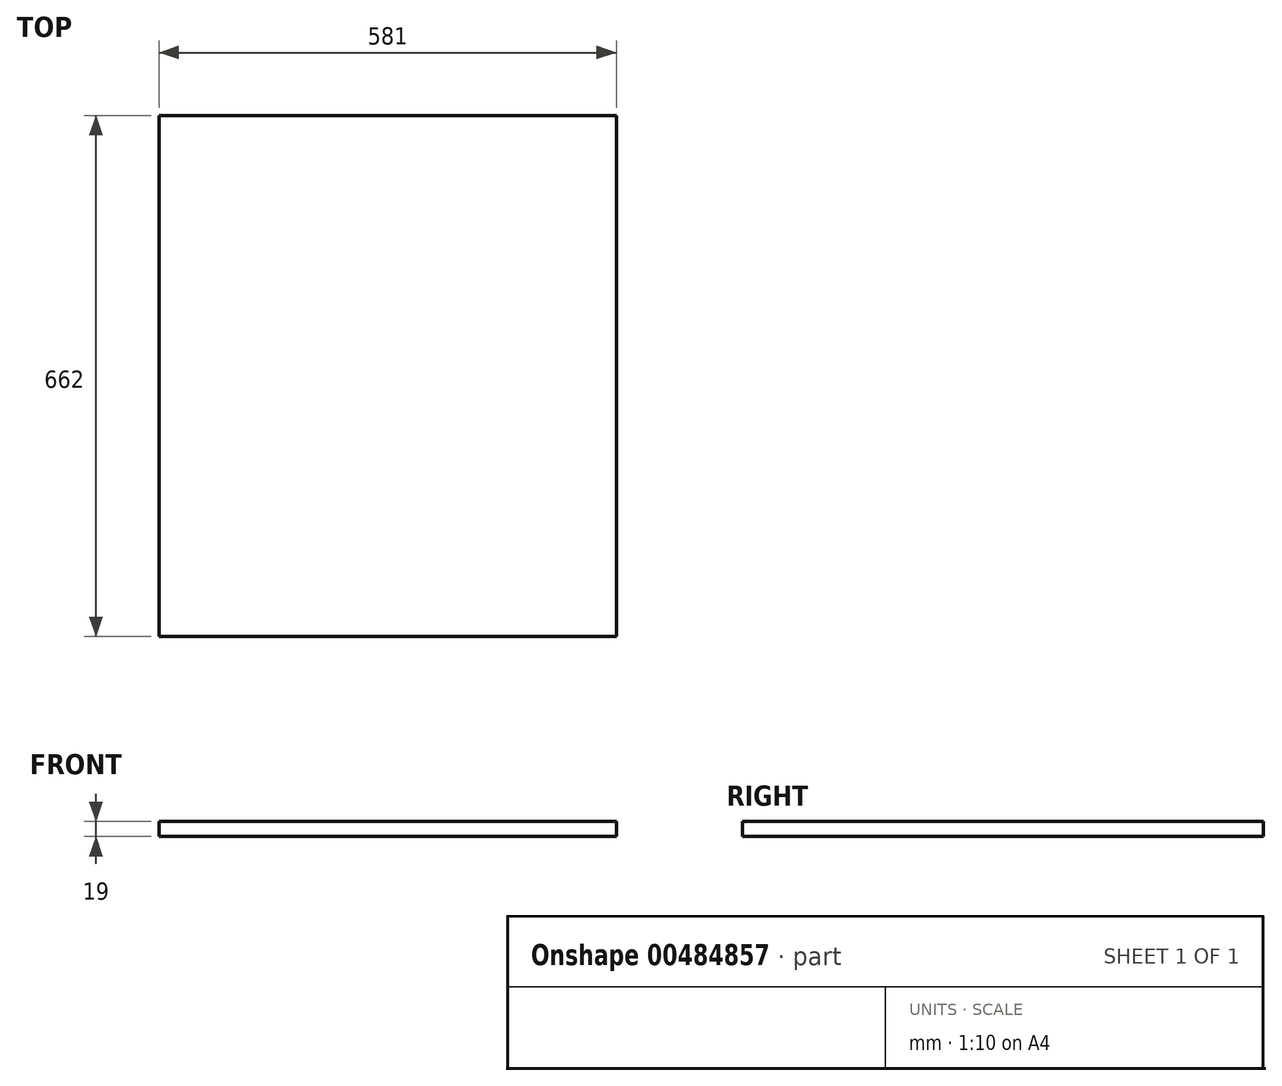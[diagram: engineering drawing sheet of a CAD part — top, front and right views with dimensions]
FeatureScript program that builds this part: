
annotation { "Feature Type Name" : "Feature", "Feature Type Description" : "" }
export const myFeature = defineFeature(function(context is Context, id is Id, definition is map)
    precondition{}
    {
        {
            var Q0;
            Q0=qCreatedBy(makeId("Top.planeOp"),FACE);
            var sketch = newSketch(context, id + "F0", { "sketchPlane" : qUnion([Q0])});
            skLineSegment(sketch, "E0.bottom", {"start": v(-289.7, 481.62) * mm, "end": v(291.3, 481.62) * mm});
            skLineSegment(sketch, "E0.top", {"start": v(-289.7, -180.38) * mm, "end": v(291.3, -180.38) * mm});
            skLineSegment(sketch, "E0.left", {"start": v(-289.7, 481.62) * mm, "end": v(-289.7, -180.38) * mm});
            skLineSegment(sketch, "E0.right", {"start": v(291.3, 481.62) * mm, "end": v(291.3, -180.38) * mm});
            skSolve(sketch);
        }
        {
            var Q0;
            Q0 = qSketchRegion(id + "F0", true);
            var Q1;
            Q1=makeQuery(id+"F0.imprint","IMPRINT",FACE,{"disambiguationData":[TD([[makeQuery(id+"F0.imprint","IMPRINT",EDGE,{"derivedFrom":sQuery(id+"F0.wireOp",EDGE,"E0.bottom")}),-1.0]])]});
            extrude(context, id + "F1", {"entities" : qUnion([Q0, Q1]), "depth" : 19 * mm});
        }
    });
